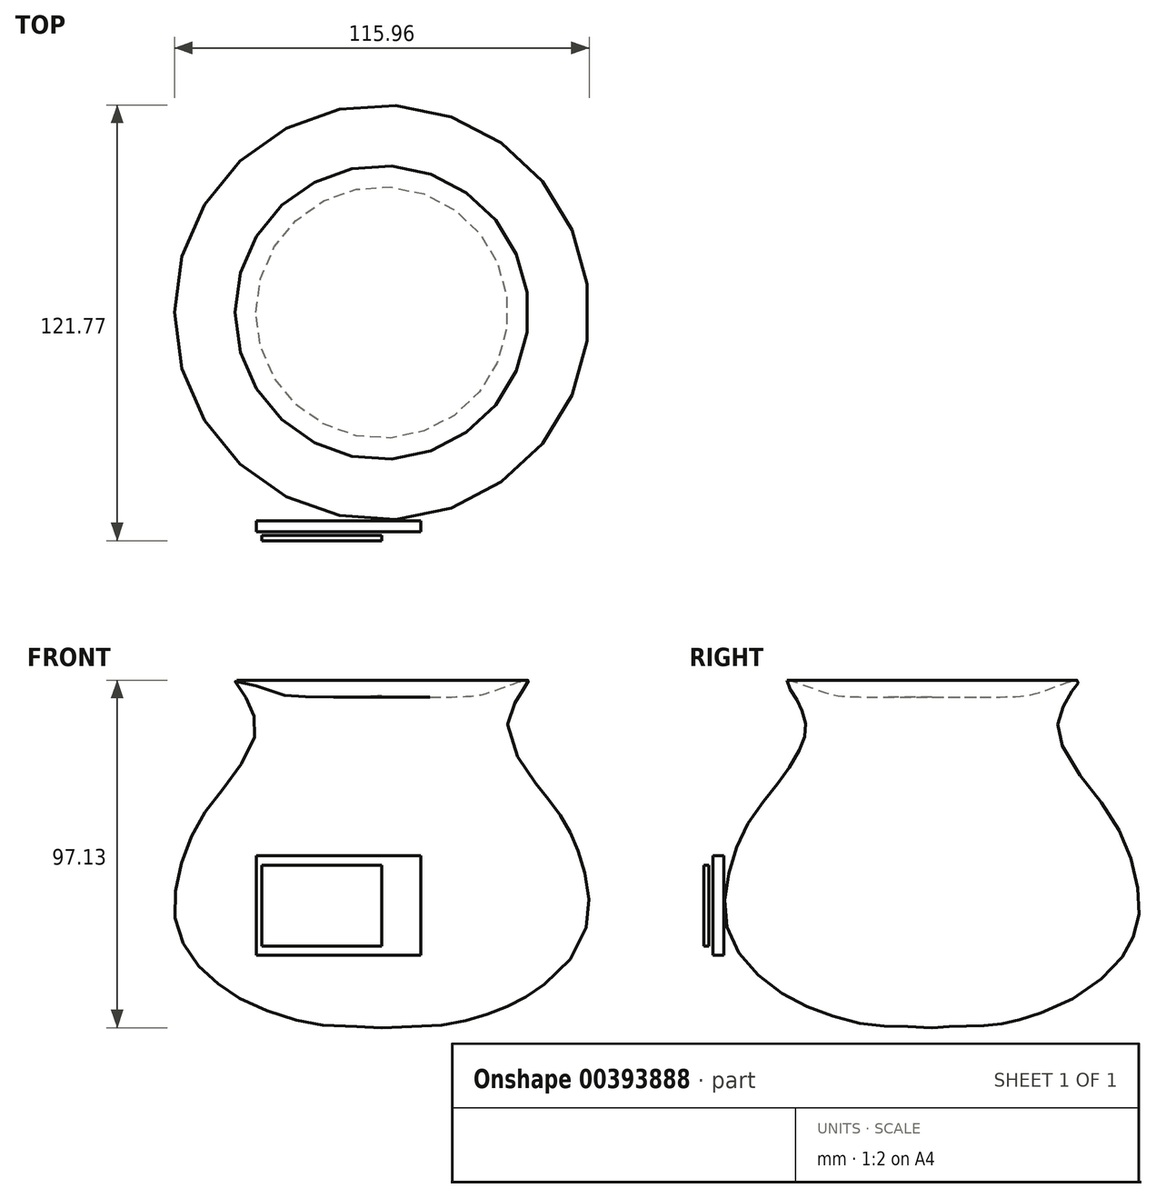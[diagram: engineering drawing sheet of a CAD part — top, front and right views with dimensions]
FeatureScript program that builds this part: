
annotation { "Feature Type Name" : "Feature", "Feature Type Description" : "" }
export const myFeature = defineFeature(function(context is Context, id is Id, definition is map)
    precondition{}
    {
        {
            var Q0;
            Q0=qCreatedBy(makeId("Front.planeOp"),FACE);
            var sketch = newSketch(context, id + "F0", { "sketchPlane" : qUnion([Q0])});
            skFitSpline(sketch, "E0", {"points": [v(0, 47.45) * mm, v(-12.65, 47) * mm, v(-23.33, 47.23) * mm, v(-30, 48.34) * mm, v(-40.91, 51.68) * mm, v(-38.91, 48.34) * mm, v(-36.02, 42.55) * mm, v(-35.35, 36.77) * mm, v(-41.36, 25.2) * mm, v(-49.15, 15.18) * mm, v(-54.5, 5.16) * mm, v(-57.6, -6.41) * mm, v(-57.38, -16.65) * mm, v(-52.7, -26.22) * mm, v(-45.37, -33.34) * mm, v(-36.68, -38.69) * mm, v(-23.55, -43.36) * mm, v(-12.2, -44.92) * mm, v(0, -45.36) * mm, v(0, -45.59) * mm, v(0, -45.8) * mm], "startDerivative": vector(-205.7, -10.31) * mm, "endDerivative": vector(3.55, -27.05) * mm});
            skLineSegment(sketch, "E1", {"start": v(0, 47.45) * mm, "end": v(0, -45.8) * mm, "construction": true});
            skLineSegment(sketch, "E2", {"start": v(0, 47.45) * mm, "end": v(0, -45.8) * mm});
            skSolve(sketch);
        }
        {
            var Q0;
            {var subQ0=sQuery(id+"F0.wireOp",EDGE,"E2");var subQ1=sQuery(id+"F0.wireOp",EDGE,"E0");var subQ2=makeQuery(id+"F0.imprint","INTERSECT",VERTEX,{"disambiguationData":[OD(0.0)],"derivedFrom":[subQ1,subQ0]});Q0=makeQuery(id+"F0.imprint","IMPRINT",FACE,{"disambiguationData":[TD([[makeQuery(id+"F0.imprint","IMPRINT",EDGE,{"disambiguationData":[TD([[subQ2,-1.0]])],"derivedFrom":subQ1}),1.0]])]});}
            var Q1;
            Q1=sQuery(id+"F0.wireOp",EDGE,"E1");
            revolve(context, id + "F1", {"entities" : qUnion([Q0]), "axis" : qUnion([Q1]), "revolveType" : RevolveType.FULL});
        }
        {
            var Q0;
            Q0=qCreatedBy(makeId("Front.planeOp"),FACE);
            var sketch = newSketch(context, id + "F2", { "sketchPlane" : qUnion([Q0])});
            skLineSegment(sketch, "E3", {"start": v(-27.27, -44.3) * mm, "end": v(-48.06, -44.3) * mm});
            skLineSegment(sketch, "E4", {"start": v(-48.06, -44.3) * mm, "end": v(-48.06, -39.66) * mm});
            skLineSegment(sketch, "E5", {"start": v(-48.06, -39.66) * mm, "end": v(-27.27, -44.3) * mm});
            skSolve(sketch);
        }
        {
            var Q0;
            Q0=makeQuery(id+"F2.imprint","IMPRINT",FACE,{"disambiguationData":[TD([[makeQuery(id+"F2.imprint","IMPRINT",EDGE,{"derivedFrom":sQuery(id+"F2.wireOp",EDGE,"E3")}),-1.0]])]});
            extrude(context, id + "F3", {"entities" : qUnion([Q0]), "depth" : 0.25 * mm});
        }
        {
            var Q0;
            Q0=makeQuery(id+"F3.opExtrude","SWEPT_BODY",BODY,{"disambiguationData":[OSD([sQuery(id+"F2.wireOp",EDGE,"E3"),sQuery(id+"F2.wireOp",EDGE,"E4"),sQuery(id+"F2.wireOp",EDGE,"E5")])]});
            deleteBodies(context, id + "F4", {"entities" : qUnion([Q0])});
        }
        {
            var Q0;
            Q0=qCreatedBy(makeId("Front.planeOp"),FACE);
            cPlane(context, id + "F5", {"entities" : qUnion([Q0]), "cplaneType" : CPlaneType.OFFSET, "offset" : 58.2 * mm, "width" : 152.4 * mm, "height" : 152.4 * mm});
        }
        {
            var Q0;
            Q0=qCreatedBy(id+"F5.planeOp",FACE);
            var sketch = newSketch(context, id + "F6", { "sketchPlane" : qUnion([Q0])});
            skLineSegment(sketch, "E6.bottom", {"start": v(-35.12, 2.67) * mm, "end": v(10.9, 2.67) * mm});
            skLineSegment(sketch, "E6.top", {"start": v(-35.12, -25.11) * mm, "end": v(10.9, -25.11) * mm});
            skLineSegment(sketch, "E6.left", {"start": v(-35.12, 2.67) * mm, "end": v(-35.12, -25.11) * mm});
            skLineSegment(sketch, "E6.right", {"start": v(10.9, 2.67) * mm, "end": v(10.9, -25.11) * mm});
            skSolve(sketch);
        }
        {
            var Q0;
            Q0=makeQuery(id+"F6.imprint","IMPRINT",FACE,{"disambiguationData":[TD([[makeQuery(id+"F6.imprint","IMPRINT",EDGE,{"derivedFrom":sQuery(id+"F6.wireOp",EDGE,"E6.bottom")}),-1.0]])]});
            extrude(context, id + "F7", {"entities" : qUnion([Q0]), "depth" : 3.05 * mm});
        }
        {
            var Q0;
            Q0=makeQuery(id+"F7.opExtrude","CAP_FACE",FACE,{"disambiguationData":[OSD([sQuery(id+"F6.wireOp",EDGE,"E6.bottom"),sQuery(id+"F6.wireOp",EDGE,"E6.top"),sQuery(id+"F6.wireOp",EDGE,"E6.left"),sQuery(id+"F6.wireOp",EDGE,"E6.right")])],"isStart":false});
            var sketch = newSketch(context, id + "F8", { "sketchPlane" : qUnion([Q0])});
            skSolve(sketch);
        }
        {
            var Q0;
            Q0=makeQuery(id+"F8.imprint","IMPRINT",FACE,{"disambiguationData":[TD([[makeQuery(id+"F8.imprint","IMPRINT",EDGE,{"derivedFrom":makeQuery(id+"F7.opExtrude","CAP_EDGE",EDGE,{"disambiguationData":[OSD([sQuery(id+"F6.wireOp",EDGE,"E6.bottom")])],"isStart":false})}),-1.0]])]});
            var sketch = newSketch(context, id + "F9", { "sketchPlane" : qUnion([Q0])});
            skCircle(sketch, "E7", {"center": v(4.9, -5.78) * mm, "radius": 3.6 * mm});
            skCircle(sketch, "E8", {"center": v(5.11, -19.56) * mm, "radius": 3.68 * mm});
            skCircle(sketch, "E9", {"center": v(5.11, -12.9) * mm, "radius": 1.2 * mm});
            skSolve(sketch);
        }
        {
            var Q0;
            Q0=sQuery(id+"F9.wireOp",EDGE,"E7");
            extrude(context, id + "F10", {"bodyType" : ToolBodyType.SURFACE, "surfaceEntities" : qUnion([Q0]), "depth" : 2.54 * mm});
        }
        {
            var Q0;
            Q0=makeQuery(id+"F8.imprint","IMPRINT",FACE,{"disambiguationData":[TD([[makeQuery(id+"F8.imprint","IMPRINT",EDGE,{"derivedFrom":makeQuery(id+"F7.opExtrude","CAP_EDGE",EDGE,{"disambiguationData":[OSD([sQuery(id+"F6.wireOp",EDGE,"E6.bottom")])],"isStart":false})}),-1.0]])]});
            var sketch = newSketch(context, id + "F11", { "sketchPlane" : qUnion([Q0])});
            skCircle(sketch, "E10", {"center": v(4.94, -18) * mm, "radius": 3.62 * mm});
            skSolve(sketch);
        }
        {
            var Q0;
            Q0=sQuery(id+"F11.wireOp",EDGE,"E10");
            extrude(context, id + "F12", {"bodyType" : ToolBodyType.SURFACE, "surfaceEntities" : qUnion([Q0]), "depth" : 2.03 * mm});
        }
        {
            var Q0;
            Q0=makeQuery(id+"F8.imprint","IMPRINT",FACE,{"disambiguationData":[TD([[makeQuery(id+"F8.imprint","IMPRINT",EDGE,{"derivedFrom":makeQuery(id+"F7.opExtrude","CAP_EDGE",EDGE,{"disambiguationData":[OSD([sQuery(id+"F6.wireOp",EDGE,"E6.bottom")])],"isStart":false})}),-1.0]])]});
            cPlane(context, id + "F13", {"entities" : qUnion([Q0]), "cplaneType" : CPlaneType.OFFSET, "offset" : 1.02 * mm, "width" : 152.4 * mm, "height" : 152.4 * mm});
        }
        {
            var Q0;
            Q0=qCreatedBy(id+"F13.planeOp",FACE);
            var sketch = newSketch(context, id + "F14", { "sketchPlane" : qUnion([Q0])});
            skLineSegment(sketch, "E11.bottom", {"start": v(-33.58, 0) * mm, "end": v(0, 0) * mm});
            skLineSegment(sketch, "E11.top", {"start": v(-33.58, -22.6) * mm, "end": v(0, -22.6) * mm});
            skLineSegment(sketch, "E11.left", {"start": v(-33.58, 0) * mm, "end": v(-33.58, -22.6) * mm});
            skLineSegment(sketch, "E11.right", {"start": v(0, 0) * mm, "end": v(0, -22.6) * mm});
            skSolve(sketch);
        }
        {
            var Q0;
            Q0=makeQuery(id+"F14.imprint","IMPRINT",FACE,{"disambiguationData":[TD([[makeQuery(id+"F14.imprint","IMPRINT",EDGE,{"derivedFrom":sQuery(id+"F14.wireOp",EDGE,"E11.bottom")}),-1.0]])]});
            extrude(context, id + "F15", {"entities" : qUnion([Q0]), "depth" : 1.52 * mm});
        }
    });
